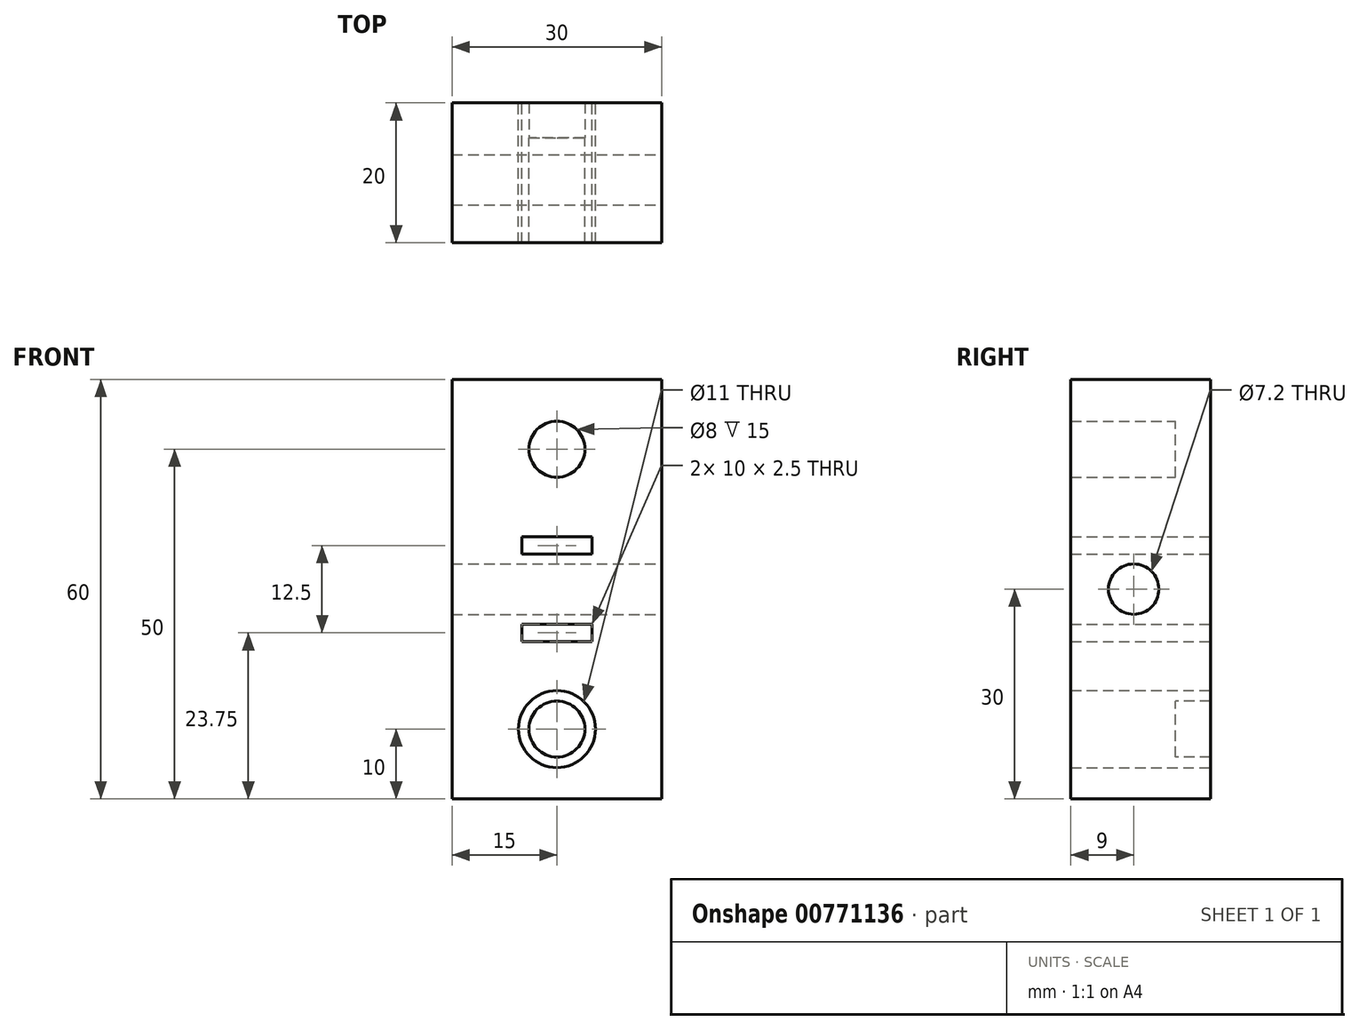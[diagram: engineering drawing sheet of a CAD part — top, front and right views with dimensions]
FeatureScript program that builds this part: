
annotation { "Feature Type Name" : "Feature", "Feature Type Description" : "" }
export const myFeature = defineFeature(function(context is Context, id is Id, definition is map)
    precondition{}
    {
        {
            var Q0;
            Q0=qCreatedBy(makeId("Front.planeOp"),FACE);
            var sketch = newSketch(context, id + "F0", { "sketchPlane" : qUnion([Q0])});
            skLineSegment(sketch, "E0.bottom", {"start": v(15, -30) * mm, "end": v(-15, -30) * mm});
            skLineSegment(sketch, "E0.top", {"start": v(15, 30) * mm, "end": v(-15, 30) * mm});
            skLineSegment(sketch, "E0.left", {"start": v(15, -30) * mm, "end": v(15, 30) * mm});
            skLineSegment(sketch, "E0.right", {"start": v(-15, -30) * mm, "end": v(-15, 30) * mm});
            skPoint(sketch, "E0.middle", {"position": v(0, 0) * mm});
            skCircle(sketch, "E1", {"center": v(0, 20) * mm, "radius": 5.5 * mm});
            skLineSegment(sketch, "E2.bottom", {"start": v(5, 5) * mm, "end": v(-5, 5) * mm});
            skLineSegment(sketch, "E2.top", {"start": v(5, 7.5) * mm, "end": v(-5, 7.5) * mm});
            skLineSegment(sketch, "E2.left", {"start": v(5, 5) * mm, "end": v(5, 7.5) * mm});
            skLineSegment(sketch, "E2.right", {"start": v(-5, 5) * mm, "end": v(-5, 7.5) * mm});
            skPoint(sketch, "E2.middle", {"position": v(0, 6.25) * mm});
            skLineSegment(sketch, "E3.MirrorCS", {"start": v(-5, -5) * mm, "end": v(-5, -7.5) * mm});
            skLineSegment(sketch, "E4.MirrorCS", {"start": v(5, -5) * mm, "end": v(5, -7.5) * mm});
            skLineSegment(sketch, "E5.MirrorCS", {"start": v(5, -7.5) * mm, "end": v(-5, -7.5) * mm});
            skLineSegment(sketch, "E6.MirrorCS", {"start": v(5, -5) * mm, "end": v(-5, -5) * mm});
            skCircle(sketch, "E7.MirrorC", {"center": v(0, -20) * mm, "radius": 5.5 * mm});
            skPoint(sketch, "E8.MirrorP", {"position": v(0, -6.25) * mm});
            skCircle(sketch, "E9", {"center": v(0, 20) * mm, "radius": 4 * mm});
            skCircle(sketch, "E10", {"center": v(0, -20) * mm, "radius": 4 * mm});
            skSolve(sketch);
        }
        {
            var Q0;
            Q0=makeQuery(id+"F0.imprint","IMPRINT",FACE,{"disambiguationData":[TD([[makeQuery(id+"F0.imprint","IMPRINT",EDGE,{"derivedFrom":sQuery(id+"F0.wireOp",EDGE,"E0.bottom")}),-1.0]])]});
            var Q1;
            Q1=makeQuery(id+"F0.imprint","IMPRINT",FACE,{"disambiguationData":[TD([[makeQuery(id+"F0.imprint","IMPRINT",EDGE,{"derivedFrom":sQuery(id+"F0.wireOp",EDGE,"E1")}),1.0]])]});
            var Q2;
            Q2=makeQuery(id+"F0.imprint","IMPRINT",FACE,{"disambiguationData":[TD([[makeQuery(id+"F0.imprint","IMPRINT",EDGE,{"derivedFrom":sQuery(id+"F0.wireOp",EDGE,"E7.MirrorC")}),-1.0]])]});
            extrude(context, id + "F1", {"entities" : qUnion([Q0, Q1, Q2]), "depth" : 5 * mm, "offsetDistance" : 25 * mm});
        }
        {
            var Q0;
            Q0=makeQuery(id+"F0.imprint","IMPRINT",FACE,{"disambiguationData":[TD([[makeQuery(id+"F0.imprint","IMPRINT",EDGE,{"derivedFrom":sQuery(id+"F0.wireOp",EDGE,"E1")}),1.0]])]});
            var Q1;
            Q1=makeQuery(id+"F0.imprint","IMPRINT",FACE,{"disambiguationData":[TD([[makeQuery(id+"F0.imprint","IMPRINT",EDGE,{"derivedFrom":sQuery(id+"F0.wireOp",EDGE,"E7.MirrorC")}),-1.0]])]});
            var Q2;
            Q2=makeQuery(id+"F0.imprint","IMPRINT",FACE,{"disambiguationData":[TD([[makeQuery(id+"F0.imprint","IMPRINT",EDGE,{"derivedFrom":sQuery(id+"F0.wireOp",EDGE,"E9")}),1.0]])]});
            var Q3;
            Q3=makeQuery(id+"F0.imprint","IMPRINT",FACE,{"disambiguationData":[TD([[makeQuery(id+"F0.imprint","IMPRINT",EDGE,{"derivedFrom":sQuery(id+"F0.wireOp",EDGE,"E10")}),1.0]])]});
            var Q4;
            Q4=sQuery(id+"F0.wireOp",EDGE,"E1");
            var Q5;
            Q5=sQuery(id+"F0.wireOp",EDGE,"E7.MirrorC");
            extrude(context, id + "F2", {"entities" : qUnion([Q0, Q1, Q2, Q3]), "operationType" : NewBodyOperationType.ADD, "surfaceEntities" : qUnion([Q4, Q5]), "oppositeDirection" : true, "depth" : 15 * mm, "offsetDistance" : 25 * mm});
        }
        {
            var Q0;
            Q0=qCreatedBy(makeId("Right.planeOp"),FACE);
            var sketch = newSketch(context, id + "F3", { "sketchPlane" : qUnion([Q0])});
            skCircle(sketch, "E11", {"center": v(4, 0) * mm, "radius": 3.6 * mm});
            skLineSegment(sketch, "E12.bottom", {"start": v(0, 5) * mm, "end": v(10, 5) * mm});
            skLineSegment(sketch, "E12.top", {"start": v(0, -5) * mm, "end": v(10, -5) * mm});
            skLineSegment(sketch, "E12.left", {"start": v(0, 5) * mm, "end": v(0, -5) * mm});
            skLineSegment(sketch, "E12.right", {"start": v(10, 5) * mm, "end": v(10, -5) * mm});
            skSolve(sketch);
        }
        {
            var Q0;
            Q0 = qSketchRegion(id + "F3", true);
            var Q1;
            Q1=makeQuery(id+"F3.imprint","IMPRINT",FACE,{"disambiguationData":[TD([[makeQuery(id+"F3.imprint","IMPRINT",EDGE,{"derivedFrom":sQuery(id+"F3.wireOp",EDGE,"E11")}),1.0]])]});
            extrude(context, id + "F4", {"entities" : qUnion([Q0, Q1]), "operationType" : NewBodyOperationType.ADD, "endBound" : BoundingType.SYMMETRIC, "depth" : 30 * mm, "offsetDistance" : 25 * mm});
        }
        {
            var Q0;
            Q0=makeQuery(id+"F3.imprint","IMPRINT",FACE,{"disambiguationData":[TD([[makeQuery(id+"F3.imprint","IMPRINT",EDGE,{"derivedFrom":sQuery(id+"F3.wireOp",EDGE,"E11")}),1.0]])]});
            extrude(context, id + "F5", {"entities" : qUnion([Q0]), "operationType" : NewBodyOperationType.REMOVE, "endBound" : BoundingType.SYMMETRIC, "oppositeDirection" : true, "depth" : 50 * mm, "offsetDistance" : 25 * mm});
        }
        {
            var Q0;
            Q0=makeQuery(id+"F0.imprint","IMPRINT",FACE,{"disambiguationData":[TD([[makeQuery(id+"F0.imprint","IMPRINT",EDGE,{"derivedFrom":sQuery(id+"F0.wireOp",EDGE,"E9")}),1.0]])]});
            var Q1;
            Q1=makeQuery(id+"F0.imprint","IMPRINT",FACE,{"disambiguationData":[TD([[makeQuery(id+"F0.imprint","IMPRINT",EDGE,{"derivedFrom":sQuery(id+"F0.wireOp",EDGE,"E10")}),1.0]])]});
            extrude(context, id + "F6", {"entities" : qUnion([Q0, Q1]), "operationType" : NewBodyOperationType.REMOVE, "endBound" : BoundingType.SYMMETRIC, "oppositeDirection" : true, "depth" : 20 * mm, "offsetDistance" : 25 * mm});
        }
    });
